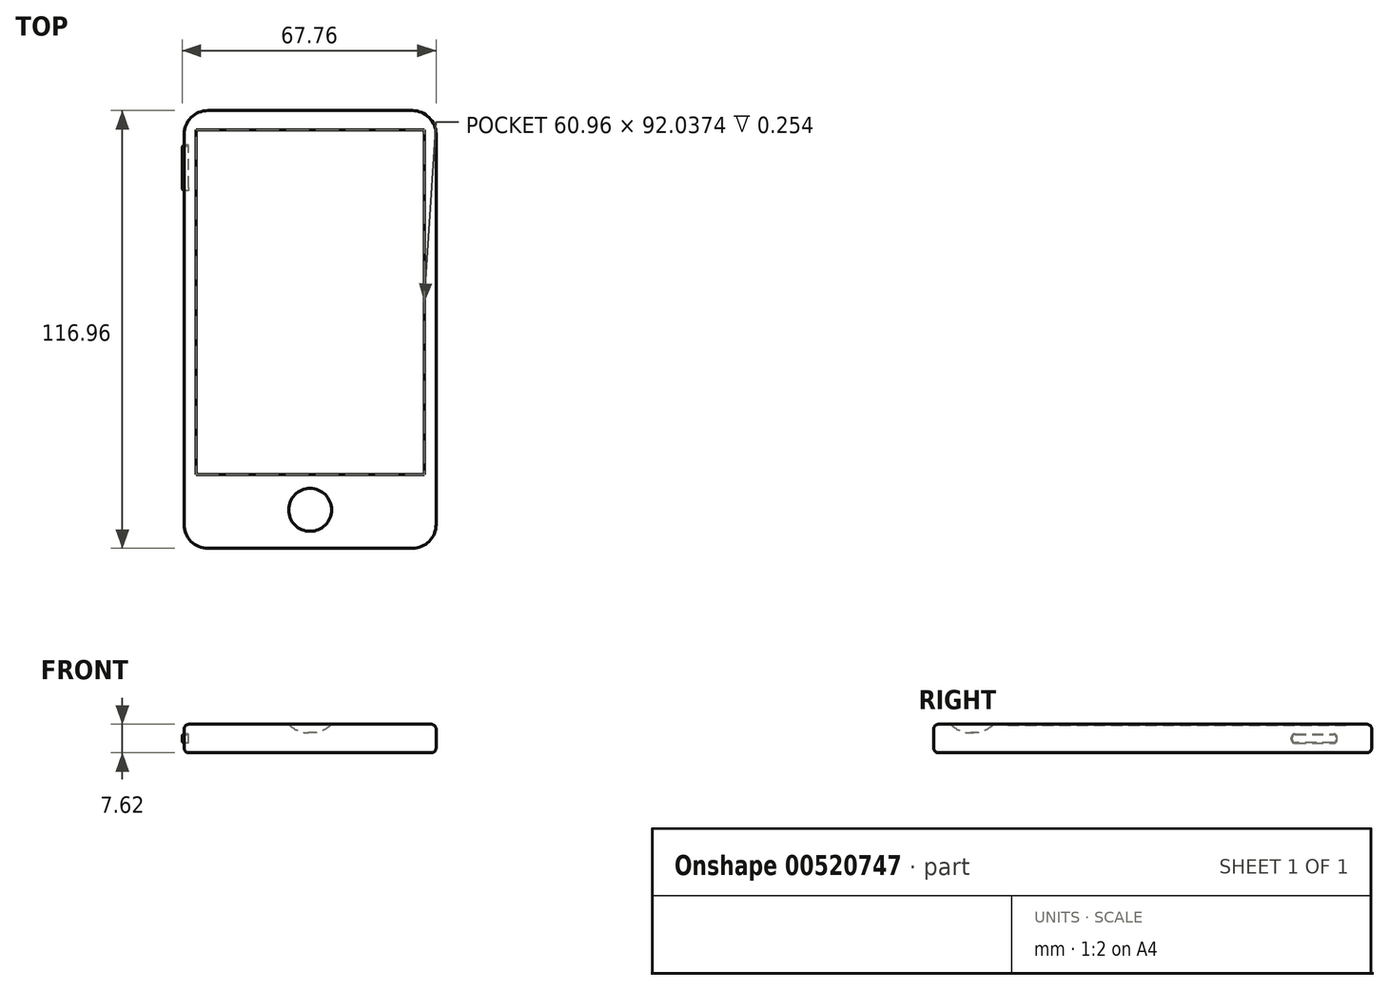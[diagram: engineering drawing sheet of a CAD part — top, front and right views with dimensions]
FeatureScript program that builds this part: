
annotation { "Feature Type Name" : "Feature", "Feature Type Description" : "" }
export const myFeature = defineFeature(function(context is Context, id is Id, definition is map)
    precondition{}
    {
        {
            var Q0;
            Q0=qCreatedBy(makeId("Top.planeOp"),FACE);
            var sketch = newSketch(context, id + "F0", { "sketchPlane" : qUnion([Q0])});
            skLineSegment(sketch, "E0.bottom", {"start": v(27.29, -58.48) * mm, "end": v(-27.29, -58.48) * mm});
            skLineSegment(sketch, "E0.top", {"start": v(27.29, 58.48) * mm, "end": v(-27.29, 58.48) * mm});
            skLineSegment(sketch, "E0.left", {"start": v(33.64, -52.13) * mm, "end": v(33.64, 52.13) * mm});
            skLineSegment(sketch, "E0.right", {"start": v(-33.64, -52.13) * mm, "end": v(-33.64, 52.13) * mm});
            skPoint(sketch, "E0.middle", {"position": v(0, 0) * mm});
            skPoint(sketch, "E1.visualSharp", {"position": v(33.64, 58.48) * mm});
            skArc(sketch, "E1.filletArc", {"start": v(33.64, 52.13) * mm, "mid": v(31.78, 56.62) * mm, "end": v(27.29, 58.48) * mm});
            skPoint(sketch, "E2.visualSharp", {"position": v(-33.64, 58.48) * mm});
            skArc(sketch, "E2.filletArc", {"start": v(-27.29, 58.48) * mm, "mid": v(-31.78, 56.62) * mm, "end": v(-33.64, 52.13) * mm});
            skPoint(sketch, "E3.visualSharp", {"position": v(-33.64, -58.48) * mm});
            skArc(sketch, "E3.filletArc", {"start": v(-33.64, -52.13) * mm, "mid": v(-31.78, -56.62) * mm, "end": v(-27.29, -58.48) * mm});
            skPoint(sketch, "E4.visualSharp", {"position": v(33.64, -58.48) * mm});
            skArc(sketch, "E4.filletArc", {"start": v(27.29, -58.48) * mm, "mid": v(31.78, -56.62) * mm, "end": v(33.64, -52.13) * mm});
            skSolve(sketch);
        }
        {
            var Q0;
            Q0=makeQuery(id+"F0.imprint","IMPRINT",FACE,{"disambiguationData":[TD([[makeQuery(id+"F0.imprint","IMPRINT",EDGE,{"derivedFrom":sQuery(id+"F0.wireOp",EDGE,"E0.bottom")}),-1.0]])]});
            extrude(context, id + "F1", {"entities" : qUnion([Q0]), "endBound" : BoundingType.SYMMETRIC, "depth" : 7.62 * mm, "offsetDistance" : 25.4 * mm});
        }
        {
            var Q0;
            Q0=makeQuery(id+"F1.opExtrude","CAP_EDGE",EDGE,{"disambiguationData":[OSD([sQuery(id+"F0.wireOp",EDGE,"E0.left")])],"isStart":false});
            var Q1;
            Q1=makeQuery(id+"F1.opExtrude","CAP_EDGE",EDGE,{"disambiguationData":[OSD([sQuery(id+"F0.wireOp",EDGE,"E0.left")])],"isStart":true});
            fillet(context, id + "F2", {"entities" : qUnion([Q0, Q1]), "radius" : 1.27 * mm, "tangentPropagation" : true, "allowEdgeOverflow" : false});
        }
        {
            var Q0;
            Q0=makeQuery(id+"F1.opExtrude","CAP_FACE",FACE,{"disambiguationData":[OSD([sQuery(id+"F0.wireOp",EDGE,"E0.bottom"),sQuery(id+"F0.wireOp",EDGE,"E0.top"),sQuery(id+"F0.wireOp",EDGE,"E0.left"),sQuery(id+"F0.wireOp",EDGE,"E0.right"),sQuery(id+"F0.wireOp",EDGE,"E1.filletArc"),sQuery(id+"F0.wireOp",EDGE,"E2.filletArc"),sQuery(id+"F0.wireOp",EDGE,"E3.filletArc"),sQuery(id+"F0.wireOp",EDGE,"E4.filletArc")])],"isStart":false});
            var sketch = newSketch(context, id + "F3", { "sketchPlane" : qUnion([Q0])});
            skLineSegment(sketch, "E5.top", {"start": v(30.48, 53.34) * mm, "end": v(-30.48, 53.34) * mm});
            skLineSegment(sketch, "E5.left", {"start": v(30.48, -38.7) * mm, "end": v(30.48, 53.34) * mm});
            skLineSegment(sketch, "E5.right", {"start": v(-30.48, -38.7) * mm, "end": v(-30.48, 53.34) * mm});
            skPoint(sketch, "E5.middle", {"position": v(0, 0) * mm});
            skLineSegment(sketch, "E6", {"start": v(-30.48, -38.7) * mm, "end": v(30.48, -38.7) * mm});
            skPoint(sketch, "E7.orphan", {"position": v(30.48, -53.34) * mm});
            skPoint(sketch, "E8.orphan", {"position": v(-30.48, -53.34) * mm});
            skCircle(sketch, "E9", {"center": v(0, -48.2) * mm, "radius": 5.73 * mm});
            skSolve(sketch);
        }
        {
            var Q0;
            Q0=makeQuery(id+"F3.imprint","IMPRINT",FACE,{"disambiguationData":[TD([[makeQuery(id+"F3.imprint","IMPRINT",EDGE,{"derivedFrom":sQuery(id+"F3.wireOp",EDGE,"E9")}),1.0]])]});
            extrude(context, id + "F4", {"entities" : qUnion([Q0]), "operationType" : NewBodyOperationType.REMOVE, "oppositeDirection" : true, "depth" : 2.3 * mm, "offsetDistance" : 25.4 * mm});
        }
        {
            var Q0;
            Q0=makeQuery(id+"F4.boolean.opBoolean","COPY",EDGE,{"derivedFrom":makeQuery(id+"F4.opExtrude","CAP_EDGE",EDGE,{"disambiguationData":[OSD([sQuery(id+"F3.wireOp",EDGE,"E9")])],"isStart":false})});
            fillet(context, id + "F5", {"entities" : qUnion([Q0]), "radius" : 7.3 * mm, "tangentPropagation" : true, "allowEdgeOverflow" : false});
        }
        {
            var Q0;
            Q0=makeQuery(id+"F3.imprint","IMPRINT",FACE,{"disambiguationData":[TD([[makeQuery(id+"F3.imprint","IMPRINT",EDGE,{"derivedFrom":sQuery(id+"F3.wireOp",EDGE,"E5.top")}),1.0]])]});
            extrude(context, id + "F6", {"entities" : qUnion([Q0]), "operationType" : NewBodyOperationType.REMOVE, "oppositeDirection" : true, "depth" : 0.25 * mm, "offsetDistance" : 25.4 * mm});
        }
        {
            var Q0;
            Q0=makeQuery(id+"F1.opExtrude","SWEPT_FACE",FACE,{"disambiguationData":[OSD([sQuery(id+"F0.wireOp",EDGE,"E0.right")])]});
            var sketch = newSketch(context, id + "F7", { "sketchPlane" : qUnion([Q0])});
            skLineSegment(sketch, "E10.bottom", {"start": v(-37.08, -1.25) * mm, "end": v(-49.23, -1.25) * mm});
            skLineSegment(sketch, "E10.top", {"start": v(-37.08, 1.25) * mm, "end": v(-49.23, 1.25) * mm});
            skLineSegment(sketch, "E10.left", {"start": v(-37.08, -1.25) * mm, "end": v(-37.08, 1.25) * mm});
            skLineSegment(sketch, "E10.right", {"start": v(-49.23, -1.25) * mm, "end": v(-49.23, 1.25) * mm});
            skPoint(sketch, "E10.middle", {"position": v(-43.16, 0) * mm});
            skSolve(sketch);
        }
        {
            var Q0;
            Q0=makeQuery(id+"F7.imprint","IMPRINT",FACE,{"disambiguationData":[TD([[makeQuery(id+"F7.imprint","IMPRINT",EDGE,{"derivedFrom":sQuery(id+"F7.wireOp",EDGE,"E10.bottom")}),-1.0]])]});
            extrude(context, id + "F8", {"entities" : qUnion([Q0]), "operationType" : NewBodyOperationType.REMOVE, "oppositeDirection" : true, "depth" : 1.12 * mm, "offsetDistance" : 25.4 * mm});
        }
        {
            var Q0;
            Q0=makeQuery(id+"F8.boolean.opBoolean","COPY",EDGE,{"derivedFrom":makeQuery(id+"F8.opExtrude","SWEPT_EDGE",EDGE,{"disambiguationData":[OSD([sQuery(id+"F7.wireOp",EDGE,"E10.top"),sQuery(id+"F7.wireOp",EDGE,"E10.left")])]})});
            var Q1;
            Q1=makeQuery(id+"F8.boolean.opBoolean","COPY",EDGE,{"derivedFrom":makeQuery(id+"F8.opExtrude","SWEPT_EDGE",EDGE,{"disambiguationData":[OSD([sQuery(id+"F7.wireOp",EDGE,"E10.top"),sQuery(id+"F7.wireOp",EDGE,"E10.right")])]})});
            var Q2;
            Q2=makeQuery(id+"F8.boolean.opBoolean","COPY",EDGE,{"derivedFrom":makeQuery(id+"F8.opExtrude","SWEPT_EDGE",EDGE,{"disambiguationData":[OSD([sQuery(id+"F7.wireOp",EDGE,"E10.bottom"),sQuery(id+"F7.wireOp",EDGE,"E10.right")])]})});
            var Q3;
            Q3=makeQuery(id+"F8.boolean.opBoolean","COPY",EDGE,{"derivedFrom":makeQuery(id+"F8.opExtrude","SWEPT_EDGE",EDGE,{"disambiguationData":[OSD([sQuery(id+"F7.wireOp",EDGE,"E10.bottom"),sQuery(id+"F7.wireOp",EDGE,"E10.left")])]})});
            fillet(context, id + "F9", {"entities" : qUnion([Q0, Q1, Q2, Q3]), "radius" : 0.92 * mm, "tangentPropagation" : true, "allowEdgeOverflow" : false});
        }
        {
            var Q0;
            Q0=makeQuery(id+"F8.boolean.opBoolean","COPY",FACE,{"derivedFrom":makeQuery(id+"F8.opExtrude","CAP_FACE",FACE,{"disambiguationData":[OSD([sQuery(id+"F7.wireOp",EDGE,"E10.bottom"),sQuery(id+"F7.wireOp",EDGE,"E10.top"),sQuery(id+"F7.wireOp",EDGE,"E10.left"),sQuery(id+"F7.wireOp",EDGE,"E10.right")])],"isStart":false})});
            var sketch = newSketch(context, id + "F10", { "sketchPlane" : qUnion([Q0])});
            skArc(sketch, "E11.0", {"start": v(-38, -1.07) * mm, "mid": v(-37.47, -0.85) * mm, "end": v(-37.26, -0.33) * mm});
            skLineSegment(sketch, "E11.1", {"start": v(-48.31, -1.07) * mm, "end": v(-38, -1.07) * mm});
            skLineSegment(sketch, "E11.2", {"start": v(-37.26, -0.33) * mm, "end": v(-37.26, 0.33) * mm});
            skArc(sketch, "E11.3", {"start": v(-49.05, -0.33) * mm, "mid": v(-48.84, -0.85) * mm, "end": v(-48.31, -1.07) * mm});
            skArc(sketch, "E11.4", {"start": v(-37.26, 0.33) * mm, "mid": v(-37.47, 0.85) * mm, "end": v(-38, 1.07) * mm});
            skLineSegment(sketch, "E11.5", {"start": v(-38, 1.07) * mm, "end": v(-48.31, 1.07) * mm});
            skArc(sketch, "E11.6", {"start": v(-48.31, 1.07) * mm, "mid": v(-48.84, 0.85) * mm, "end": v(-49.05, 0.33) * mm});
            skLineSegment(sketch, "E11.7", {"start": v(-49.05, 0.33) * mm, "end": v(-49.05, -0.33) * mm});
            skSolve(sketch);
        }
        {
            var Q0;
            Q0=makeQuery(id+"F10.imprint","IMPRINT",FACE,{"disambiguationData":[TD([[makeQuery(id+"F10.imprint","IMPRINT",EDGE,{"derivedFrom":sQuery(id+"F10.wireOp",EDGE,"E11.0")}),1.0]])]});
            extrude(context, id + "F11", {"entities" : qUnion([Q0]), "depth" : 1.6 * mm, "offsetDistance" : 25.4 * mm});
        }
        {
            var Q0;
            Q0=makeQuery(id+"F11.opExtrude","CAP_EDGE",EDGE,{"disambiguationData":[OSD([sQuery(id+"F10.wireOp",EDGE,"E11.0")])],"isStart":false});
            var Q1;
            Q1=makeQuery(id+"F11.opExtrude","CAP_EDGE",EDGE,{"disambiguationData":[OSD([sQuery(id+"F10.wireOp",EDGE,"E11.2")])],"isStart":false});
            var Q2;
            Q2=makeQuery(id+"F11.opExtrude","CAP_EDGE",EDGE,{"disambiguationData":[OSD([sQuery(id+"F10.wireOp",EDGE,"E11.4")])],"isStart":false});
            var Q3;
            Q3=makeQuery(id+"F11.opExtrude","CAP_EDGE",EDGE,{"disambiguationData":[OSD([sQuery(id+"F10.wireOp",EDGE,"E11.5")])],"isStart":false});
            var Q4;
            Q4=makeQuery(id+"F11.opExtrude","CAP_EDGE",EDGE,{"disambiguationData":[OSD([sQuery(id+"F10.wireOp",EDGE,"E11.6")])],"isStart":false});
            var Q5;
            Q5=makeQuery(id+"F11.opExtrude","CAP_EDGE",EDGE,{"disambiguationData":[OSD([sQuery(id+"F10.wireOp",EDGE,"E11.7")])],"isStart":false});
            var Q6;
            Q6=makeQuery(id+"F11.opExtrude","CAP_EDGE",EDGE,{"disambiguationData":[OSD([sQuery(id+"F10.wireOp",EDGE,"E11.3")])],"isStart":false});
            var Q7;
            Q7=makeQuery(id+"F11.opExtrude","CAP_EDGE",EDGE,{"disambiguationData":[OSD([sQuery(id+"F10.wireOp",EDGE,"E11.1")])],"isStart":false});
            fillet(context, id + "F12", {"entities" : qUnion([Q0, Q1, Q2, Q3, Q4, Q5, Q6, Q7]), "radius" : 0.3 * mm, "tangentPropagation" : true, "allowEdgeOverflow" : false});
        }
    });
